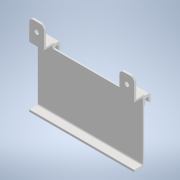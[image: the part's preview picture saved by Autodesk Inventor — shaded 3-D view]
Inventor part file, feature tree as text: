
AUTODESK INVENTOR PART (.ipt)
format: ipt  version: 2022 (Build 260153000, 153)  size: 399,360 bytes
history: native  units: mm
features: reference x25, other x10, fillet x6, extrude x5, sketch x5, projected_geometry x3, mirror x1
ambient origin geometry x8: Origin, YZ Plane, XZ Plane, XY Plane, X Axis, Y Axis, Z Axis, Center Point
bodies: Body1 (feature_tree)
feature tree (55):
  other  "Твердое тело1"
  extrude  "Выдавливание1"  Depth=1.5mm
  extrude  "Выдавливание2"  Depth=2.0mm TaperAngle=0.0deg
  other  "РабПлоскость1"
  extrude  "Выдавливание3"  Depth=2.0mm TaperAngle=0.0deg
  fillet  "Сопряжение1"  Radius=6.452mm
  extrude  "Выдавливание4"  Depth=0.3mm
  fillet  "Сопряжение2"  Radius=1.0mm
  other  "РабПлоскость2"
  extrude  "Выдавливание11"  Depth=1.5mm TaperAngle=0.0deg
  fillet  "Сопряжение9"  Radius=3.2mm
  fillet  "Сопряжение10"  Radius=3.2mm
  fillet  "Сопряжение11"  Radius=3.0mm
  mirror  "Зеркальное отражение1"
  fillet  "Сопряжение12"  Radius=8.0mm
  sketch  "Эскиз1"
  reference  "Ссылка1"
  reference  "Ссылка2"
  reference  "Ссылка3"
  sketch  "Эскиз2"
  projected_geometry  "Спроецированная петля1"
  sketch  "Эскиз3"
  projected_geometry  "Спроецированная петля2"
  reference  "Ссылка4"
  reference  "Ссылка5"
  reference  "Ссылка6"
  reference  "Ссылка7"
  reference  "Ссылка8"
  reference  "Ссылка9"
  sketch  "Эскиз4"
  reference  "Ссылка10"
  reference  "Ссылка11"
  projected_geometry  "Спроецированная петля3"
  reference  "Ссылка12"
  reference  "Ссылка13"
  reference  "Ссылка14"
  reference  "Ссылка15"
  reference  "Ссылка16"
  reference  "Ссылка19"
  sketch  "Эскиз11"
  reference  "Ссылка20"
  reference  "Ссылка21"
  reference  "Ссылка22"
  reference  "Ссылка23"
  reference  "Ссылка24"
  reference  "Ссылка25"
  reference  "Ссылка26"
  reference  "Ссылка27"
  other  "<userpath>\Documents\Git\MZCAT_2024\MZCAT_3.iam"
  other  "MZCAT_3.iam"
  other  "commutationCATboard:1"
  other  "CAT_protector:1"
  other  "vydacha_slide:1"
  other  "base plate:2"
  other  "base:1"
